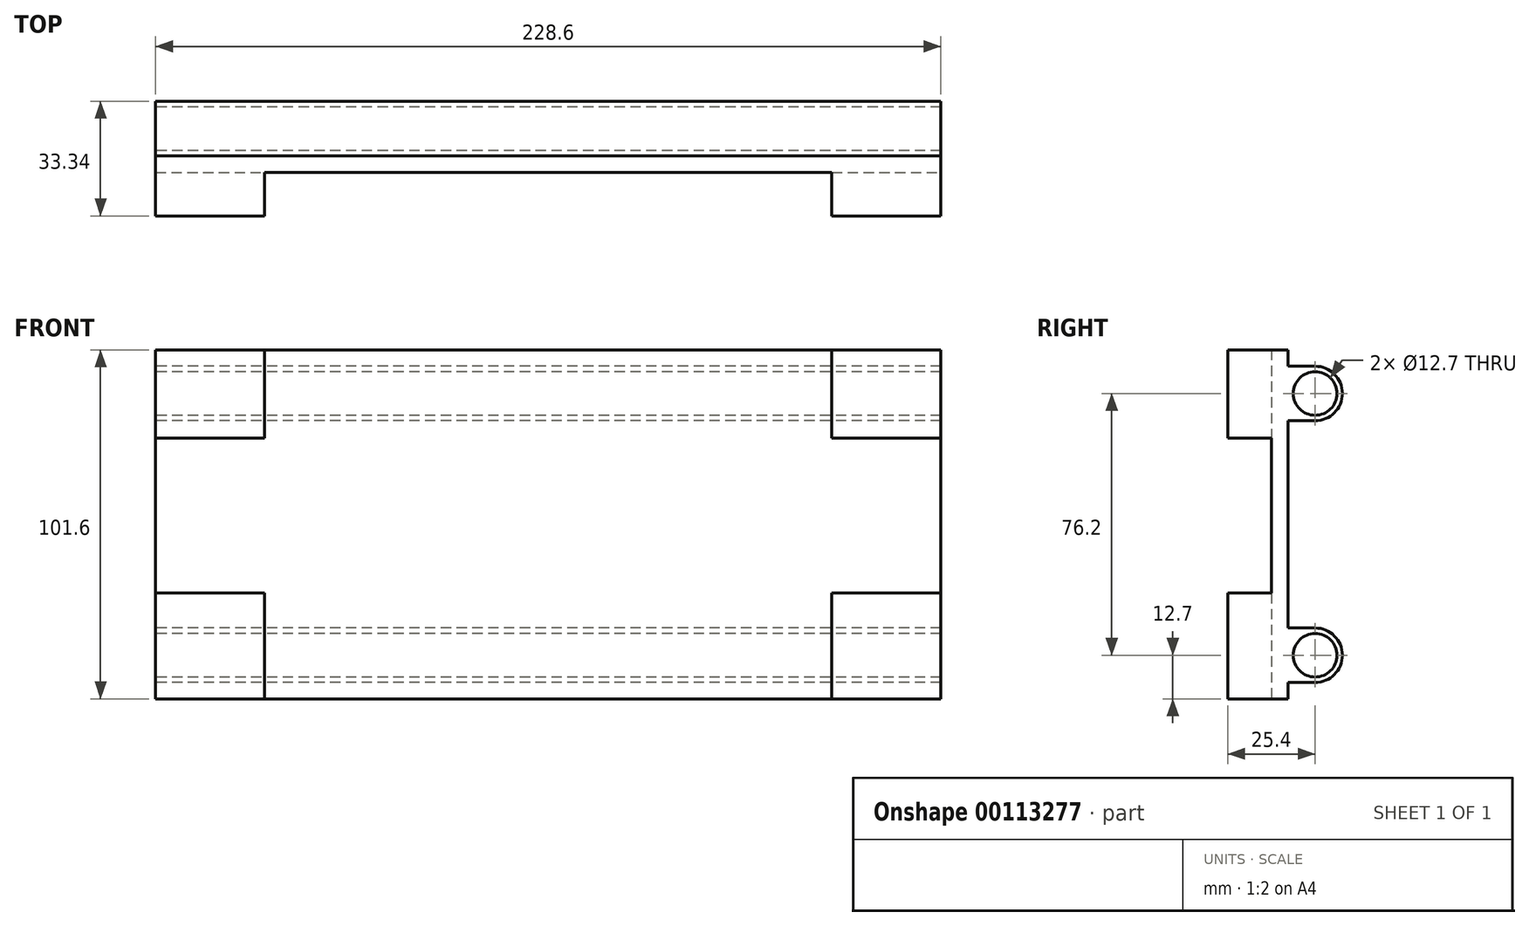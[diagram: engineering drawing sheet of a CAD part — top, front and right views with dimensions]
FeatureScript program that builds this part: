
annotation { "Feature Type Name" : "Feature", "Feature Type Description" : "" }
export const myFeature = defineFeature(function(context is Context, id is Id, definition is map)
    precondition{}
    {
        {
            var Q0;
            Q0=qCreatedBy(makeId("Right.planeOp"),FACE);
            var sketch = newSketch(context, id + "F0", { "sketchPlane" : qUnion([Q0])});
            skCircle(sketch, "E0", {"center": v(0, 38.1) * mm, "radius": 6.35 * mm});
            skCircle(sketch, "E1", {"center": v(0, -38.1) * mm, "radius": 6.35 * mm});
            skCircle(sketch, "E2", {"center": v(0, 38.1) * mm, "radius": 7.94 * mm});
            skCircle(sketch, "E3", {"center": v(0, -38.1) * mm, "radius": 7.94 * mm});
            skLineSegment(sketch, "E4.bottom", {"start": v(-7.94, 50.8) * mm, "end": v(-25.4, 50.8) * mm});
            skLineSegment(sketch, "E4.top", {"start": v(-7.94, -50.8) * mm, "end": v(-25.4, -50.8) * mm});
            skLineSegment(sketch, "E4.left", {"start": v(-7.94, 50.8) * mm, "end": v(-7.94, 46.04) * mm});
            skLineSegment(sketch, "E4.right", {"start": v(-25.4, 50.8) * mm, "end": v(-25.4, -50.8) * mm});
            skLineSegment(sketch, "E5", {"start": v(-7.94, 46.04) * mm, "end": v(0, 46.04) * mm});
            skLineSegment(sketch, "E6", {"start": v(-7.94, -46.04) * mm, "end": v(0, -46.04) * mm});
            skLineSegment(sketch, "E7", {"start": v(0, 30.16) * mm, "end": v(-7.94, 30.16) * mm});
            skLineSegment(sketch, "E8", {"start": v(0, -30.16) * mm, "end": v(-7.94, -30.16) * mm});
            skLineSegment(sketch, "E9.trimOffspring", {"start": v(-7.94, -46.04) * mm, "end": v(-7.94, -50.8) * mm});
            skLineSegment(sketch, "E10.trimOffspring", {"start": v(-7.94, 30.16) * mm, "end": v(-7.94, -30.16) * mm});
            skSolve(sketch);
        }
        {
            var Q0;
            Q0=makeQuery(id+"F0.imprint","IMPRINT",FACE,{"disambiguationData":[TD([[makeQuery(id+"F0.imprint","IMPRINT",EDGE,{"derivedFrom":sQuery(id+"F0.wireOp",EDGE,"E4.bottom")}),1.0]])]});
            var Q1;
            Q1=makeQuery(id+"F0.imprint","IMPRINT",FACE,{"disambiguationData":[TD([[makeQuery(id+"F0.imprint","IMPRINT",EDGE,{"derivedFrom":sQuery(id+"F0.wireOp",EDGE,"E1")}),-1.0]])]});
            var Q2;
            Q2=makeQuery(id+"F0.imprint","IMPRINT",FACE,{"disambiguationData":[TD([[makeQuery(id+"F0.imprint","IMPRINT",EDGE,{"derivedFrom":sQuery(id+"F0.wireOp",EDGE,"E0")}),-1.0]])]});
            extrude(context, id + "F1", {"entities" : qUnion([Q0, Q1, Q2]), "depth" : 228.6 * mm});
        }
        {
            var Q0;
            Q0=makeQuery(id+"F1.opExtrude","SWEPT_FACE",FACE,{"disambiguationData":[OSD([sQuery(id+"F0.wireOp",EDGE,"E4.right")])]});
            var sketch = newSketch(context, id + "F2", { "sketchPlane" : qUnion([Q0])});
            skLineSegment(sketch, "E11.bottom", {"start": v(31.75, 61.14) * mm, "end": v(196.85, 61.14) * mm});
            skLineSegment(sketch, "E11.top", {"start": v(31.75, -65.86) * mm, "end": v(196.85, -65.86) * mm});
            skLineSegment(sketch, "E11.left", {"start": v(31.75, 61.14) * mm, "end": v(31.75, -65.86) * mm});
            skLineSegment(sketch, "E11.right", {"start": v(196.85, 61.14) * mm, "end": v(196.85, -65.86) * mm});
            skLineSegment(sketch, "E12.bottom", {"start": v(-39.36, 25.06) * mm, "end": v(272.27, 25.06) * mm});
            skLineSegment(sketch, "E12.top", {"start": v(-39.36, -20.03) * mm, "end": v(272.27, -20.03) * mm});
            skLineSegment(sketch, "E12.left", {"start": v(-39.36, 25.06) * mm, "end": v(-39.36, -20.03) * mm});
            skLineSegment(sketch, "E12.right", {"start": v(272.27, 25.06) * mm, "end": v(272.27, -20.03) * mm});
            skSolve(sketch);
        }
        {
            var Q0;
            {var subQ0=sQuery(id+"F2.wireOp",EDGE,"E12.bottom");var subQ1=sQuery(id+"F2.wireOp",EDGE,"E11.left");var subQ2=makeQuery(id+"F2.imprint","INTERSECT",VERTEX,{"derivedFrom":[subQ1,subQ0]});Q0=makeQuery(id+"F2.imprint","IMPRINT",FACE,{"disambiguationData":[TD([[makeQuery(id+"F2.imprint","IMPRINT",EDGE,{"disambiguationData":[TD([[subQ2,-1.0]])],"derivedFrom":subQ0}),1.0]])]});}
            var Q1;
            {var subQ0=sQuery(id+"F2.wireOp",EDGE,"E11.bottom");Q1=makeQuery(id+"F2.imprint","IMPRINT",FACE,{"disambiguationData":[TD([[makeQuery(id+"F2.imprint","IMPRINT",EDGE,{"derivedFrom":subQ0}),-1.0]])]});}
            var Q2;
            {var subQ0=sQuery(id+"F2.wireOp",EDGE,"E12.bottom");var subQ1=sQuery(id+"F2.wireOp",EDGE,"E11.left");var subQ2=makeQuery(id+"F2.imprint","INTERSECT",VERTEX,{"derivedFrom":[subQ1,subQ0]});Q2=makeQuery(id+"F2.imprint","IMPRINT",FACE,{"disambiguationData":[TD([[makeQuery(id+"F2.imprint","IMPRINT",EDGE,{"disambiguationData":[TD([[subQ2,-1.0]])],"derivedFrom":subQ1}),1.0]])]});}
            var Q3;
            {var subQ0=sQuery(id+"F2.wireOp",EDGE,"E12.top");var subQ1=sQuery(id+"F2.wireOp",EDGE,"E11.left");var subQ2=makeQuery(id+"F2.imprint","INTERSECT",VERTEX,{"derivedFrom":[subQ1,subQ0]});Q3=makeQuery(id+"F2.imprint","IMPRINT",FACE,{"disambiguationData":[TD([[makeQuery(id+"F2.imprint","IMPRINT",EDGE,{"disambiguationData":[TD([[subQ2,-1.0]])],"derivedFrom":subQ0}),-1.0]])]});}
            var Q4;
            {var subQ0=sQuery(id+"F2.wireOp",EDGE,"E11.top");Q4=makeQuery(id+"F2.imprint","IMPRINT",FACE,{"disambiguationData":[TD([[makeQuery(id+"F2.imprint","IMPRINT",EDGE,{"derivedFrom":subQ0}),1.0]])]});}
            var Q5;
            {var subQ0=sQuery(id+"F2.wireOp",EDGE,"E12.bottom");var subQ1=sQuery(id+"F2.wireOp",EDGE,"E11.left");var subQ2=makeQuery(id+"F2.imprint","INTERSECT",VERTEX,{"derivedFrom":[subQ1,subQ0]});Q5=makeQuery(id+"F2.imprint","IMPRINT",FACE,{"disambiguationData":[TD([[makeQuery(id+"F2.imprint","IMPRINT",EDGE,{"disambiguationData":[TD([[subQ2,-1.0]])],"derivedFrom":subQ1}),-1.0]])]});}
            var Q6;
            {var subQ0=sQuery(id+"F2.wireOp",EDGE,"E12.bottom");var subQ1=sQuery(id+"F2.wireOp",EDGE,"E11.right");var subQ2=makeQuery(id+"F2.imprint","INTERSECT",VERTEX,{"derivedFrom":[subQ1,subQ0]});Q6=makeQuery(id+"F2.imprint","IMPRINT",FACE,{"disambiguationData":[TD([[makeQuery(id+"F2.imprint","IMPRINT",EDGE,{"disambiguationData":[TD([[subQ2,-1.0]])],"derivedFrom":subQ1}),1.0]])]});}
            extrude(context, id + "F3", {"entities" : qUnion([Q0, Q1, Q2, Q3, Q4, Q5, Q6]), "operationType" : NewBodyOperationType.REMOVE, "oppositeDirection" : true, "depth" : 12.7 * mm});
        }
    });
